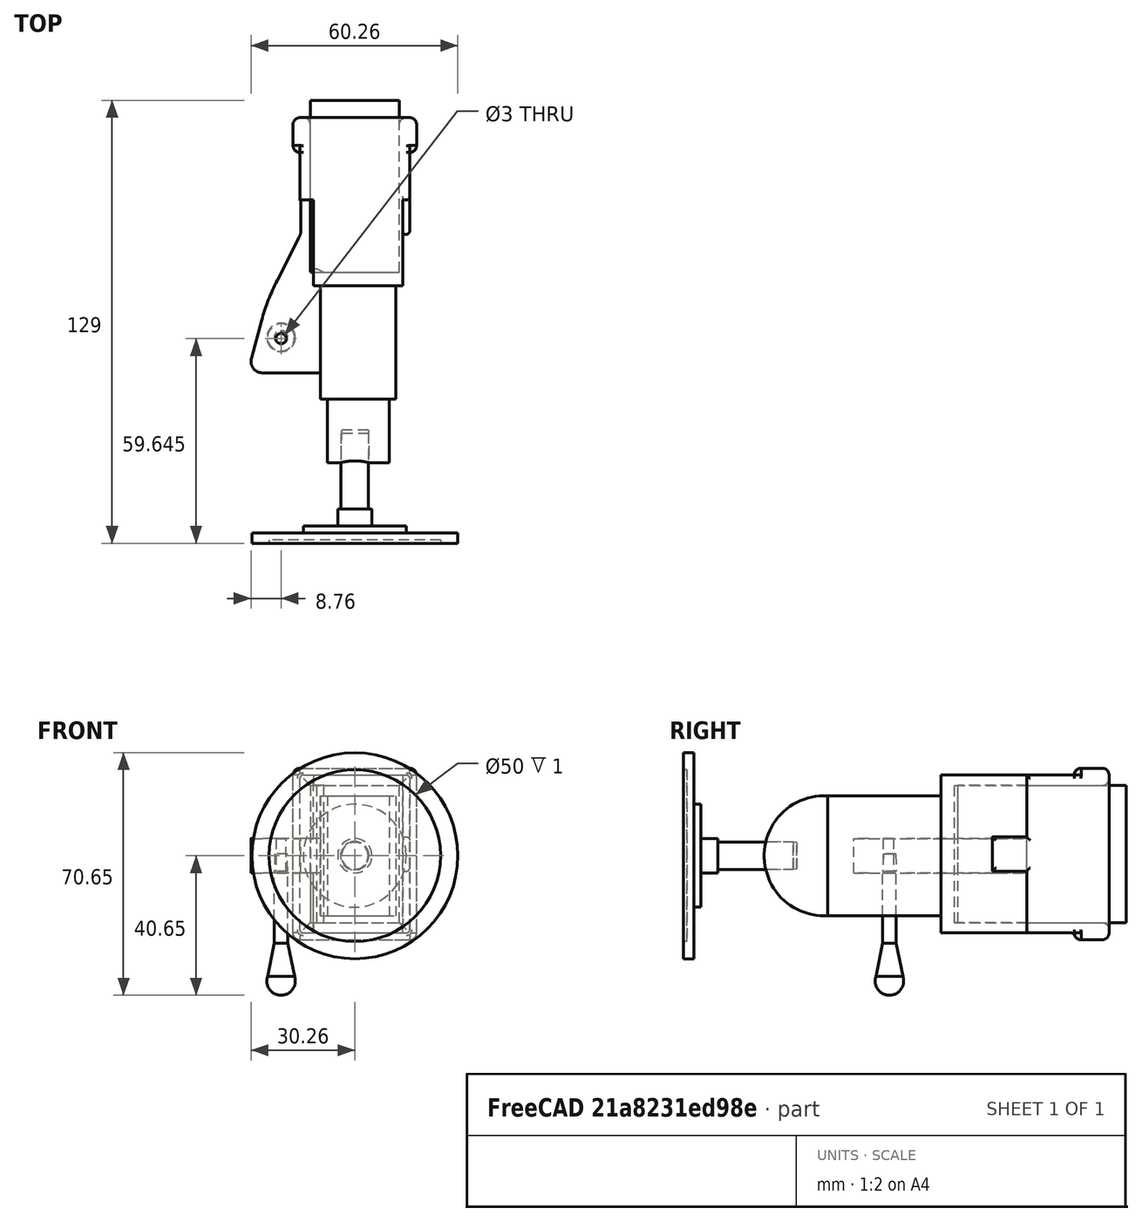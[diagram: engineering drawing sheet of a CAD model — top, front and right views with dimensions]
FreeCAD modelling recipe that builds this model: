
FCSTD DOCUMENT  (FreeCAD 0.16R6662 (Git))
Label: qtippholder-jw-rounded2-rot-fuss
License: All rights reserved
LicenseURL: http://en.wikipedia.org/wiki/All_rights_reserved
objects: Part::Cylinder×7, Part::Box×6, Sketcher::SketchObject×3, Part::Cone×3, Part::MultiFuse×3, App::DocumentObjectGroup×3, Part::Cut×3, Part::Fillet×2, Mesh::Feature×1, PartDesign::Pad×1, Part::Sphere×1, PartDesign::Pocket×1, Part::Revolution×1
note: 33 computed .brp shape members not serialized (recipe doc carries the construction recipe); baked Part::Feature solids carry a one-line shape summary decoded from their .brp

FEATURE [Mesh::Feature] EarClnrHldr
  Placement = pos=(1.7939,1.69608,-3.31283) rot=(0,0,1;0rad)
FEATURE [Part::Box] Box  label="hut"
  Height = 50
  Length = 36
  Placement = pos=(14,116,11) rot=(0,0,1;0rad)
  Width = 10
FEATURE [Part::Box] Box001  label="stirn"
  Height = 46
  Length = 32
  Placement = pos=(16,102,13) rot=(0,0,1;0rad)
  Width = 17
FEATURE [Part::Box] Box002  label="gnack"
  Height = 10
  Length = 26
  Placement = pos=(22,92,31) rot=(0,0,1;0rad)
  Width = 12
FEATURE [Part::Box] Box003  label="augen"
  Height = 46
  Length = 26
  Placement = pos=(20,77,13) rot=(0,0,1;0rad)
  Width = 26
FEATURE [Part::Box] Box004  label="wangen"
  Height = 35
  Length = 22
  Placement = pos=(22,44,18) rot=(0,0,1;0rad)
  Width = 36
FEATURE [Part::Cylinder] Cylinder  label="kinn"
  Angle = 360
  Height = 18
  Placement = pos=(24,43,35.5) rot=(0,1,0;1.5708rad)
  Radius = 17.5
FEATURE [Sketcher::SketchObject] Sketch001
  Placement = pos=(22,44,36) rot=(0,0,1;0rad)
  sketch-geometry (10):
    g0: LineSegment StartX=1.5 StartY=7.67084 StartZ=0 EndX=-16.9205 EndY=7.67084 EndZ=0
    g1: LineSegment StartX=-20.1462 StartY=11.8885 StartZ=0 EndX=-17.1712 EndY=22.8519 EndZ=0
    g2: LineSegment StartX=-12.6256 StartY=34.6 StartZ=0 EndX=-6.24014 EndY=47.0658 EndZ=0
    g3: LineSegment StartX=-5.70418 StartY=49.2877 StartZ=0 EndX=-5.70418 EndY=58.874 EndZ=0
    g4: LineSegment StartX=-5.70418 StartY=58.874 StartZ=0 EndX=1.5 EndY=58.874 EndZ=0
    g5: LineSegment StartX=1.5 StartY=58.874 StartZ=0 EndX=1.5 EndY=7.67084 EndZ=0
    g6: ArcOfCircle CenterX=-16.9205 CenterY=11.0132 CenterZ=0 NormalX=0 NormalY=0 NormalZ=1 Radius=3.34236 StartAngle=2.87662 EndAngle=4.71239
    g7: ArcOfCircle CenterX=41.2664 CenterY=6.99453 CenterZ=0 NormalX=0 NormalY=0 NormalZ=1 Radius=60.5508 StartAngle=2.6682 EndAngle=2.87662
    g8: ArcOfCircle CenterX=-10.5778 CenterY=49.2877 CenterZ=0 NormalX=0 NormalY=0 NormalZ=1 Radius=4.87365 StartAngle=5.8098 EndAngle=6.28319
    g9: Circle CenterX=-11.5 CenterY=17.6445 CenterZ=0 NormalX=0 NormalY=0 NormalZ=1 Radius=1.5
  constraints (14):
    c: Horizontal(g0)
    c: Vertical(g3)
    c: Coincident(g3,g4)
    c: Horizontal(g4)
    c: Coincident(g4,g5)
    c: Coincident(g5,g0)
    c: Vertical(g5)
    c: Tangent(g0,g6) = 1.5708
    c: Tangent(g1,g6) = 1.5708
    c: Tangent(g1,g7) = 1.5708
    c: Tangent(g2,g7) = 1.5708
    c: Tangent(g2,g8) = -1.5708
    c: Tangent(g3,g8) = -1.5708
    c: Radius(g9) = 1.5
FEATURE [PartDesign::Pad] Pad  label="nase"
  Length = 4.5
  Length2 = 5.5
  Placement = pos=(22,44,36) rot=(0,0,1;0rad)
  Sketch = -> Sketch001
  Type = 4
FEATURE [Part::Cylinder] Cylinder002  label="bein006"
  Angle = 360
  Height = 32
  Placement = pos=(32,34,35.5) rot=(1,0,0;1.5708rad)
  Radius = 4
FEATURE [Part::Cylinder] Cylinder003  label="bein001"
  Angle = 360
  Height = 11
  Placement = pos=(32,12,35.5) rot=(1,0,0;1.5708rad)
  Radius = 5
FEATURE [Part::Cylinder] Cylinder004  label="bein002"
  Angle = 360
  Height = 4
  Placement = pos=(32,7,35.5) rot=(1,0,0;1.5708rad)
  Radius = 15
FEATURE [Part::Cylinder] Cylinder005  label="bein003"
  Angle = 360
  Height = 3
  Placement = pos=(32,5,35.5) rot=(1,0,0;1.5708rad)
  Radius = 30
FEATURE [Part::Cylinder] Cylinder006  label="bein004"
  Angle = 360
  Height = 3
  Placement = pos=(32,3,35.5) rot=(1,0,0;1.5708rad)
  Radius = 25
FEATURE [Part::Box] Box005  label="kopfloch"
  Height = 40
  Length = 26
  Placement = pos=(19,81,16) rot=(0,0,1;0rad)
  Width = 50
FEATURE [Part::Cylinder] Cylinder007  label="staebchen"
  Angle = 360
  Height = 27
  Placement = pos=(10.5,62,4) rot=(0,0,1;0rad)
  Radius = 2
FEATURE [Part::Sphere] Sphere  label="Kugel"
  Angle1 = -90
  Angle2 = 90
  Angle3 = 360
  Placement = pos=(10.5,62,-1) rot=(0,0,1;0rad)
  Radius = 4.15
FEATURE [Part::Cone] Cone  label="Kegel"
  Angle = 360
  Height = 10
  Placement = pos=(10.5,62,0) rot=(0,0,1;0rad)
  Radius1 = 4
  Radius2 = 2
FEATURE [Part::Cone] Cone001  label="Kegel001"
  Angle = 360
  Height = 5
  Placement = pos=(10.5,62,31) rot=(0,0,1;0rad)
  Radius1 = 2
  Radius2 = 1.8
FEATURE [Part::Cone] Cone002  label="beinloch001"
  Angle = 360
  Height = 11
  Placement = pos=(32,35,35.5) rot=(1,0,0;1.5708rad)
  Radius1 = 3.9
  Radius2 = 4.2
FEATURE [Part::MultiFuse] Fusion
  Shapes = -> [Box,Box001,Box002,Box003,Box004,Cylinder,Pad]
FEATURE [Part::MultiFuse] Fusion001
  Shapes = -> [Cone001,Cylinder007,Sphere,Cone]
FEATURE [App::DocumentObjectGroup] Gruppe001  label="halb-qtipp"
  Group = -> [Fusion001]
FEATURE [Part::MultiFuse] Fusion002
  Shapes = -> [Cylinder002,Cylinder003,Cylinder005,Cylinder004]
FEATURE [Part::Cut] Cut002
  Base = -> Fusion002
  Tool = -> Cylinder006
FEATURE [App::DocumentObjectGroup] Gruppe  label="bein"
  Group = -> [Cut002]
FEATURE [Sketcher::SketchObject] Sketch
  Placement = pos=(19,81,16) rot=(1,0,0;3.14159rad)
  Support = -> Box005 [Face5]
  sketch-geometry (4):
    g0: LineSegment StartX=0 StartY=0 StartZ=0 EndX=0 EndY=-1 EndZ=0
    g1: LineSegment StartX=0 StartY=-1 StartZ=0 EndX=2 EndY=-1 EndZ=0
    g2: LineSegment StartX=2 StartY=-1 StartZ=0 EndX=4 EndY=0 EndZ=0
    g3: LineSegment StartX=4 StartY=0 StartZ=0 EndX=0 EndY=0 EndZ=0
  constraints (11):
    c: Coincident(g-1,g0)
    c: PointOnObject(g0,g-2)
    c: Coincident(g0,g1)
    c: Horizontal(g1)
    c: Coincident(g1,g2)
    c: Coincident(g2,g3)
    c: Coincident(g3,g0)
    c: Horizontal(g3)
    c: DistanceY(g0,g0) = 1
    c: DistanceX(g1,g1) = 2
    c: DistanceX(g3,g3) = 4
FEATURE [PartDesign::Pocket] Pocket
  Length = 5
  Placement = pos=(19,81,16) rot=(0,0,1;0rad)
  Sketch = -> Sketch
  Type = 1
FEATURE [Part::Cut] Cut
  Base = -> Fusion
  Tool = -> Pocket
FEATURE [Part::Cut] Cut003  label="kopf"
  Base = -> Cut
  Tool = -> Cone002
FEATURE [Part::Fillet] Fillet
  Base = -> Cut003
  Edges = 14 edges r=4: [Edge90,Edge91,Edge92,Edge93,Edge94,Edge95,Edge96,Edge111,Edge119,Edge120,Edge123,Edge125,Edge126,Edge127]
FEATURE [Part::Fillet] Fillet001
  Base = -> Fillet
  Edges = 16 edges r=2: [Edge44,Edge50,Edge57,Edge116,Edge117,Edge118,Edge119,Edge120,Edge136,Edge137,Edge138,Edge139,Edge163,Edge164,Edge165,Edge166]
FEATURE [App::DocumentObjectGroup] Gruppe002  label="kopf001"
  Group = -> [Fillet001]
FEATURE [Sketcher::SketchObject] Sketch002
  sketch-geometry (16):
    g0: LineSegment StartX=0 StartY=6.07692 StartZ=0 EndX=25.6 EndY=6.07692 EndZ=0
    g1: LineSegment StartX=25.6 StartY=6.07692 StartZ=0 EndX=25.6 EndY=5.07692 EndZ=0
    g2: LineSegment StartX=25.6 StartY=5.07692 StartZ=0 EndX=31.6 EndY=5.07692 EndZ=0
    g3: LineSegment StartX=31.6 StartY=5.07692 StartZ=0 EndX=31.6 EndY=6.57692 EndZ=0
    g4: LineSegment StartX=30.1 StartY=8.07692 StartZ=0 EndX=16.1 EndY=8.07692 EndZ=0
    g5: LineSegment StartX=16.1 StartY=8.07692 StartZ=0 EndX=16.1 EndY=9.07692 EndZ=0
    g6: LineSegment StartX=14.6 StartY=10.5769 StartZ=0 EndX=7.6 EndY=10.5769 EndZ=0
    g7: LineSegment StartX=6.1 StartY=12.0769 StartZ=0 EndX=6.1 EndY=15.0769 EndZ=0
    g8: LineSegment StartX=4 StartY=17.0769 StartZ=0 EndX=4 EndY=36.8595 EndZ=0
    g9: LineSegment StartX=4 StartY=36.8595 StartZ=0 EndX=0 EndY=36.8595 EndZ=0
    g10: ArcOfCircle CenterX=5.1 CenterY=15.0769 CenterZ=0 NormalX=0 NormalY=0 NormalZ=1 Radius=1 StartAngle=0 EndAngle=1.5708
    g11: ArcOfCircle CenterX=7.6 CenterY=12.0769 CenterZ=0 NormalX=0 NormalY=0 NormalZ=1 Radius=1.5 StartAngle=3.14159 EndAngle=4.71239
    g12: ArcOfCircle CenterX=14.6 CenterY=9.07692 CenterZ=0 NormalX=0 NormalY=0 NormalZ=1 Radius=1.5 StartAngle=0 EndAngle=1.5708
    g13: ArcOfCircle CenterX=30.1 CenterY=6.57692 CenterZ=0 NormalX=0 NormalY=0 NormalZ=1 Radius=1.5 StartAngle=0 EndAngle=1.5708
    g14: LineSegment StartX=5.1 StartY=16.0769 StartZ=0 EndX=5 EndY=16.0769 EndZ=0
    g15: ArcOfCircle CenterX=5 CenterY=17.0769 CenterZ=0 NormalX=0 NormalY=0 NormalZ=1 Radius=1 StartAngle=3.14159 EndAngle=4.71239
  constraints (43):
    c: Horizontal(g0)
    c: Coincident(g0,g1)
    c: Coincident(g1,g2)
    c: Horizontal(g2)
    c: Coincident(g2,g3)
    c: Vertical(g3)
    c: Vertical(g1)
    c: Horizontal(g4)
    c: Coincident(g4,g5)
    c: Vertical(g5)
    c: Horizontal(g6)
    c: Vertical(g7)
    c: Vertical(g8)
    c: Coincident(g8,g9)
    c: Horizontal(g9)
    c: DistanceX(g9,g9) = 4
    c: Tangent(g7,g10) = -1.5708
    c: Tangent(g7,g11) = 1.5708
    c: Tangent(g6,g11) = 1.5708
    c: Tangent(g6,g12) = -1.5708
    c: Tangent(g5,g12) = -1.5708
    c: Tangent(g4,g13) = -1.5708
    c: Tangent(g3,g13) = -1.5708
    c: DistanceY(g1,g1) = 1
    c: DistanceX(g2,g2) = 6
    c: Radius(g13) = 1.5
    c: DistanceY(g3,g3) = 1.5
    c: DistanceX(g4,g4) = 14
    c: DistanceX(g6,g6) = 7
    c: Radius(g12) = 1.5
    c: Radius(g11) = 1.5
    c: DistanceY(g7,g7) = 3
    c: Radius(g10) = 1
    c: PointOnObject(g0,g-2)
    c: PointOnObject(g9,g-2)
    c: DistanceY(g5,g5) = 1
    c: Coincident(g14,g10)
    c: Horizontal(g14)
    c: Angle(g10) = 1.5708
    c: Tangent(g8,g15) = 1.5708
    c: Tangent(g14,g15) = 1.5708
    c: Radius(g15) = 1
    c: DistanceX(g14,g14) = 0.1
FEATURE [Part::Revolution] Revolve  label="fuss"
  Angle = 360
  Axis = (0,1,0)
  Base = (0,0,0)
  Placement = pos=(34,-9,35.5) rot=(0,0,1;0rad)
  Solid = true
  Source = -> Sketch002
